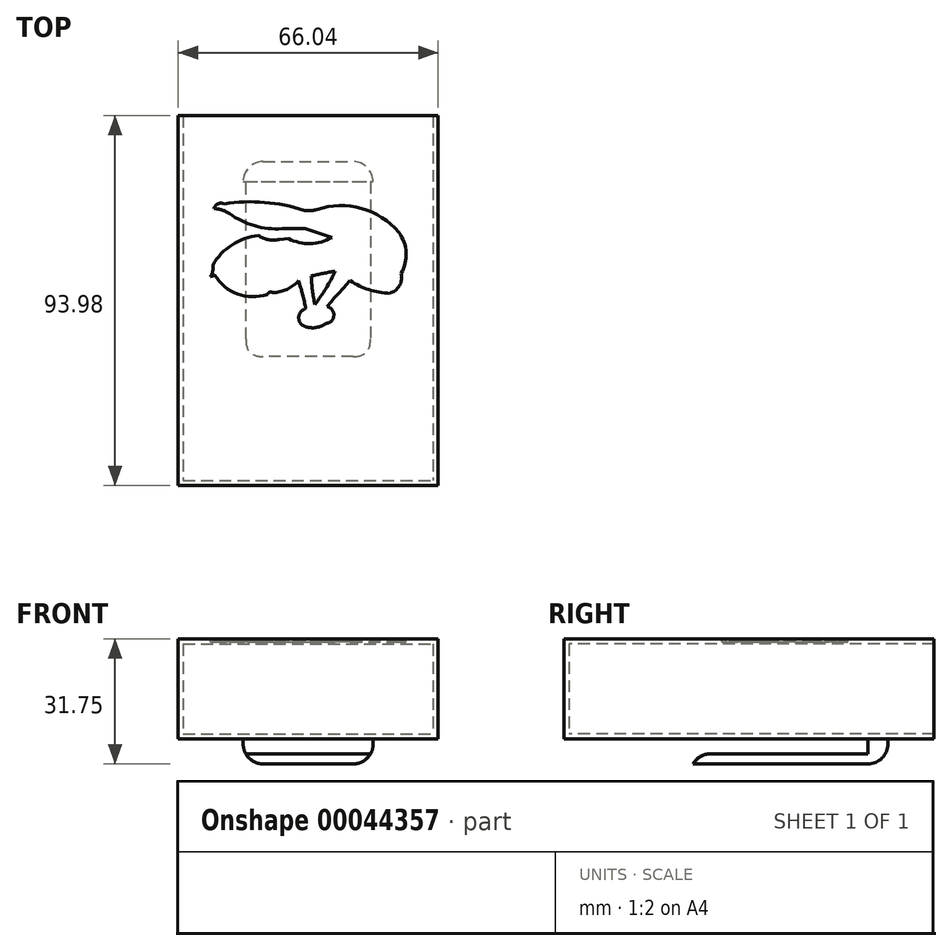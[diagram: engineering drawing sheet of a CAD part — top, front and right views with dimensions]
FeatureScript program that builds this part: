
annotation { "Feature Type Name" : "Feature", "Feature Type Description" : "" }
export const myFeature = defineFeature(function(context is Context, id is Id, definition is map)
    precondition{}
    {
        {
            var Q0;
            Q0=qCreatedBy(makeId("Top.planeOp"),FACE);
            var sketch = newSketch(context, id + "F0", { "sketchPlane" : qUnion([Q0])});
            skPoint(sketch, "E0", {"position": v(0, 0) * mm});
            skPoint(sketch, "E1", {"position": v(66.04, 0) * mm});
            skPoint(sketch, "E2", {"position": v(0, 93.98) * mm});
            skLineSegment(sketch, "E3.bottom", {"start": v(0, 93.98) * mm, "end": v(66.04, 93.98) * mm});
            skLineSegment(sketch, "E3.top", {"start": v(0, 0) * mm, "end": v(66.04, 0) * mm});
            skLineSegment(sketch, "E3.left", {"start": v(0, 93.98) * mm, "end": v(0, 0) * mm});
            skLineSegment(sketch, "E3.right", {"start": v(66.04, 93.98) * mm, "end": v(66.04, 0) * mm});
            skSolve(sketch);
        }
        {
            var Q0;
            Q0 = qSketchRegion(id + "F0", true);
            extrude(context, id + "F1", {"entities" : qUnion([Q0]), "depth" : 25.4 * mm});
        }
        {
            var Q0;
            Q0=makeQuery(id+"F1.opExtrude","SWEPT_FACE",FACE,{"disambiguationData":[OSD([sQuery(id+"F0.wireOp",EDGE,"E3.bottom")])]});
            shell(context, id + "F2", {"entities" : qUnion([Q0]), "thickness" : 1.27 * mm});
        }
        {
            var Q0;
            Q0=makeQuery(id+"F1.opExtrude","CAP_FACE",FACE,{"disambiguationData":[OSD([sQuery(id+"F0.wireOp",EDGE,"E3.bottom"),sQuery(id+"F0.wireOp",EDGE,"E3.top"),sQuery(id+"F0.wireOp",EDGE,"E3.left"),sQuery(id+"F0.wireOp",EDGE,"E3.right")])],"isStart":false});
            var sketch = newSketch(context, id + "F3", { "sketchPlane" : qUnion([Q0])});
            skPoint(sketch, "E4", {"position": v(39.02, 63.04) * mm});
            skPoint(sketch, "E5", {"position": v(25.75, 62.49) * mm});
            skPoint(sketch, "E6", {"position": v(20.37, 63.5) * mm});
            skPoint(sketch, "E7", {"position": v(28.02, 62.72) * mm});
            skPoint(sketch, "E8", {"position": v(32.23, 65.22) * mm});
            skPoint(sketch, "E9", {"position": v(13.03, 69.12) * mm});
            skPoint(sketch, "E10", {"position": v(9.05, 70.37) * mm});
            skPoint(sketch, "E11", {"position": v(11.62, 71.54) * mm});
            skPoint(sketch, "E12", {"position": v(32.08, 69.9) * mm});
            skPoint(sketch, "E13", {"position": v(56.04, 64.28) * mm});
            skPoint(sketch, "E14", {"position": v(56.66, 53.9) * mm});
            skPoint(sketch, "E15", {"position": v(53.7, 48.83) * mm});
            skPoint(sketch, "E16", {"position": v(43.7, 52.03) * mm});
            skPoint(sketch, "E17", {"position": v(39.88, 54.45) * mm});
            skPoint(sketch, "E18", {"position": v(33.8, 53.2) * mm});
            skPoint(sketch, "E19", {"position": v(34.73, 45.94) * mm});
            skPoint(sketch, "E20", {"position": v(37.85, 45.47) * mm});
            skPoint(sketch, "E21", {"position": v(37.54, 41.18) * mm});
            skPoint(sketch, "E22", {"position": v(32.39, 44.93) * mm});
            skPoint(sketch, "E23", {"position": v(32.39, 40.32) * mm});
            skPoint(sketch, "E24", {"position": v(30.6, 52.03) * mm});
            skPoint(sketch, "E25", {"position": v(24.04, 48.98) * mm});
            skPoint(sketch, "E26", {"position": v(22.65, 48.57) * mm});
            skPoint(sketch, "E27", {"position": v(9.3, 53.49) * mm});
            skPoint(sketch, "E28", {"position": v(8.22, 53.14) * mm});
            skPoint(sketch, "E29", {"position": v(8.81, 55.98) * mm});
            skArc(sketch, "E30", {"start": v(53.7, 48.83) * mm, "mid": v(56.22, 50.76) * mm, "end": v(56.66, 53.9) * mm});
            skArc(sketch, "E31", {"start": v(43.7, 52.03) * mm, "mid": v(48.48, 49.74) * mm, "end": v(53.7, 48.83) * mm});
            skArc(sketch, "E32", {"start": v(56.66, 53.9) * mm, "mid": v(57.9, 59.19) * mm, "end": v(56.04, 64.28) * mm});
            skPoint(sketch, "E33", {"position": v(35.23, 70.11) * mm});
            skArc(sketch, "E34", {"start": v(56.04, 64.28) * mm, "mid": v(46.53, 70.38) * mm, "end": v(35.23, 70.11) * mm});
            skArc(sketch, "E35", {"start": v(32.08, 69.9) * mm, "mid": v(33.67, 69.82) * mm, "end": v(35.23, 70.11) * mm});
            skArc(sketch, "E36", {"start": v(32.08, 69.9) * mm, "mid": v(21.95, 71.94) * mm, "end": v(11.62, 71.54) * mm});
            skArc(sketch, "E37", {"start": v(11.62, 71.54) * mm, "mid": v(10.07, 71.55) * mm, "end": v(9.05, 70.37) * mm});
            skArc(sketch, "E38", {"start": v(13.03, 69.12) * mm, "mid": v(11.11, 69.98) * mm, "end": v(9.05, 70.37) * mm});
            skArc(sketch, "E39", {"start": v(13.03, 69.12) * mm, "mid": v(19.35, 65.98) * mm, "end": v(26.37, 65.22) * mm});
            skLineSegment(sketch, "E40", {"start": v(26.37, 65.22) * mm, "end": v(32.23, 65.22) * mm});
            skLineSegment(sketch, "E41", {"start": v(32.23, 65.22) * mm, "end": v(39.02, 63.04) * mm});
            skArc(sketch, "E42", {"start": v(28.02, 62.72) * mm, "mid": v(33.56, 61.46) * mm, "end": v(39.02, 63.04) * mm});
            skArc(sketch, "E43", {"start": v(20.37, 63.5) * mm, "mid": v(22.96, 62.45) * mm, "end": v(25.75, 62.49) * mm});
            skLineSegment(sketch, "E44", {"start": v(25.75, 62.49) * mm, "end": v(28.02, 62.72) * mm});
            skArc(sketch, "E45", {"start": v(20.37, 63.5) * mm, "mid": v(13.68, 61.14) * mm, "end": v(8.81, 55.98) * mm});
            skArc(sketch, "E46", {"start": v(8.22, 53.14) * mm, "mid": v(8.76, 54.5) * mm, "end": v(8.81, 55.98) * mm});
            skArc(sketch, "E47", {"start": v(8.22, 53.14) * mm, "mid": v(8.78, 53.24) * mm, "end": v(9.3, 53.49) * mm});
            skArc(sketch, "E48", {"start": v(9.3, 53.49) * mm, "mid": v(15.1, 48.66) * mm, "end": v(22.65, 48.57) * mm});
            skArc(sketch, "E49", {"start": v(24.04, 48.98) * mm, "mid": v(23.25, 49.1) * mm, "end": v(22.65, 48.57) * mm});
            skArc(sketch, "E50", {"start": v(24.04, 48.98) * mm, "mid": v(27.63, 49.83) * mm, "end": v(30.6, 52.03) * mm});
            skArc(sketch, "E51", {"start": v(32.39, 44.93) * mm, "mid": v(30.61, 42.62) * mm, "end": v(32.39, 40.32) * mm});
            skArc(sketch, "E52", {"start": v(37.54, 41.18) * mm, "mid": v(39.54, 43.2) * mm, "end": v(37.85, 45.47) * mm});
            skArc(sketch, "E53", {"start": v(32.39, 40.32) * mm, "mid": v(35.07, 40.13) * mm, "end": v(37.54, 41.18) * mm});
            skArc(sketch, "E54", {"start": v(34.73, 45.94) * mm, "mid": v(37.54, 50.05) * mm, "end": v(39.88, 54.45) * mm});
            skArc(sketch, "E55", {"start": v(33.8, 53.2) * mm, "mid": v(34.12, 49.55) * mm, "end": v(34.73, 45.94) * mm});
            skArc(sketch, "E56", {"start": v(39.88, 54.45) * mm, "mid": v(36.83, 53.88) * mm, "end": v(33.8, 53.2) * mm});
            skArc(sketch, "E57", {"start": v(32.39, 44.93) * mm, "mid": v(31.63, 48.51) * mm, "end": v(30.6, 52.03) * mm});
            skArc(sketch, "E58", {"start": v(43.7, 52.03) * mm, "mid": v(40.73, 48.8) * mm, "end": v(37.85, 45.47) * mm});
            skSolve(sketch);
        }
        {
            var Q0;
            Q0 = qSketchRegion(id + "F3", true);
            extrude(context, id + "F4", {"entities" : qUnion([Q0]), "operationType" : NewBodyOperationType.REMOVE, "oppositeDirection" : true, "depth" : 0.76 * mm});
        }
        {
            var Q0;
            Q0=makeQuery(id+"F1.opExtrude","CAP_FACE",FACE,{"disambiguationData":[OSD([sQuery(id+"F0.wireOp",EDGE,"E3.bottom"),sQuery(id+"F0.wireOp",EDGE,"E3.top"),sQuery(id+"F0.wireOp",EDGE,"E3.left"),sQuery(id+"F0.wireOp",EDGE,"E3.right")])],"isStart":true});
            var sketch = newSketch(context, id + "F5", { "sketchPlane" : qUnion([Q0])});
            skPoint(sketch, "E59", {"position": v(33.02, -82.28) * mm});
            skPoint(sketch, "E59.positionSnap0", {"position": v(33.02, -93.98) * mm});
            skLineSegment(sketch, "E60", {"start": v(33.02, -93.98) * mm, "end": v(0, -93.98) * mm});
            skLineSegment(sketch, "E61", {"start": v(0, -93.98) * mm, "end": v(66.04, -93.98) * mm});
            skLineSegment(sketch, "E62", {"start": v(66.04, -93.98) * mm, "end": v(33.02, -93.98) * mm});
            skPoint(sketch, "E63", {"position": v(49.53, -93.98) * mm});
            skPoint(sketch, "E64", {"position": v(16.51, -82.28) * mm});
            skPoint(sketch, "E64.positionSnap0", {"position": v(16.51, -93.98) * mm});
            skPoint(sketch, "E65", {"position": v(49.53, -82.28) * mm});
            skPoint(sketch, "E66", {"position": v(49.53, -77.2) * mm});
            skLineSegment(sketch, "E67.bottom", {"start": v(16.51, -82.28) * mm, "end": v(49.53, -82.28) * mm});
            skLineSegment(sketch, "E67.top", {"start": v(16.51, -77.2) * mm, "end": v(49.53, -77.2) * mm});
            skLineSegment(sketch, "E67.left", {"start": v(16.51, -82.28) * mm, "end": v(16.51, -77.2) * mm});
            skLineSegment(sketch, "E67.right", {"start": v(49.53, -82.28) * mm, "end": v(49.53, -77.2) * mm});
            skSolve(sketch);
        }
        {
            var Q0;
            Q0 = qSketchRegion(id + "F5", true);
            extrude(context, id + "F6", {"entities" : qUnion([Q0]), "operationType" : NewBodyOperationType.ADD, "depth" : 3.8 * mm});
        }
        {
            var Q0;
            Q0=makeQuery(id+"F6.opExtrude","CAP_FACE",FACE,{"disambiguationData":[OSD([sQuery(id+"F5.wireOp",EDGE,"E67.bottom"),sQuery(id+"F5.wireOp",EDGE,"E67.top"),sQuery(id+"F5.wireOp",EDGE,"E67.left"),sQuery(id+"F5.wireOp",EDGE,"E67.right")])],"isStart":false});
            var sketch = newSketch(context, id + "F7", { "sketchPlane" : qUnion([Q0])});
            skPoint(sketch, "E68", {"position": v(49.53, -32.75) * mm});
            skLineSegment(sketch, "E69.bottom", {"start": v(49.53, -32.75) * mm, "end": v(16.51, -32.75) * mm});
            skLineSegment(sketch, "E69.top", {"start": v(49.53, -82.28) * mm, "end": v(16.51, -82.28) * mm});
            skLineSegment(sketch, "E69.left", {"start": v(49.53, -32.75) * mm, "end": v(49.53, -82.28) * mm});
            skLineSegment(sketch, "E69.right", {"start": v(16.51, -32.75) * mm, "end": v(16.51, -82.28) * mm});
            skSolve(sketch);
        }
        {
            var Q0;
            Q0 = qSketchRegion(id + "F7", true);
            extrude(context, id + "F8", {"entities" : qUnion([Q0]), "operationType" : NewBodyOperationType.ADD, "depth" : 2.54 * mm});
        }
        {
            var Q0;
            Q0=makeQuery(id+"F8.opExtrude","CAP_EDGE",EDGE,{"disambiguationData":[OSD([sQuery(id+"F7.wireOp",EDGE,"E69.bottom")])],"isStart":true});
            var Q1;
            Q1=makeQuery(id+"F6.opExtrude","CAP_EDGE",EDGE,{"disambiguationData":[OSD([sQuery(id+"F5.wireOp",EDGE,"E67.top")])],"isStart":false});
            fillet(context, id + "F9", {"entities" : qUnion([Q0, Q1]), "radius" : 5.08 * mm, "tangentPropagation" : true, "allowEdgeOverflow" : false});
        }
        {
            var Q0;
            Q0=makeQuery(id+"F8.boolean.opBoolean","MERGE",EDGE,{"derivedFrom":[makeQuery(id+"F6.opExtrude","SWEPT_EDGE",EDGE,{"disambiguationData":[OSD([sQuery(id+"F5.wireOp",EDGE,"E67.bottom"),sQuery(id+"F5.wireOp",EDGE,"E67.right")])]}),makeQuery(id+"F8.opExtrude","SWEPT_EDGE",EDGE,{"disambiguationData":[OSD([sQuery(id+"F7.wireOp",EDGE,"E69.top"),sQuery(id+"F7.wireOp",EDGE,"E69.left")])]})]});
            var Q1;
            Q1=makeQuery(id+"F8.opExtrude","CAP_EDGE",EDGE,{"disambiguationData":[OSD([sQuery(id+"F7.wireOp",EDGE,"E69.top")])],"isStart":false});
            var Q2;
            Q2=makeQuery(id+"F8.opExtrude","CAP_EDGE",EDGE,{"disambiguationData":[OSD([sQuery(id+"F7.wireOp",EDGE,"E69.left")])],"isStart":false});
            var Q3;
            Q3=makeQuery(id+"F8.opExtrude","CAP_EDGE",EDGE,{"disambiguationData":[OSD([sQuery(id+"F7.wireOp",EDGE,"E69.right")])],"isStart":false});
            var Q4;
            Q4=makeQuery(id+"F8.boolean.opBoolean","MERGE",EDGE,{"derivedFrom":[makeQuery(id+"F6.opExtrude","SWEPT_EDGE",EDGE,{"disambiguationData":[OSD([sQuery(id+"F5.wireOp",EDGE,"E67.bottom"),sQuery(id+"F5.wireOp",EDGE,"E67.left")])]}),makeQuery(id+"F8.opExtrude","SWEPT_EDGE",EDGE,{"disambiguationData":[OSD([sQuery(id+"F7.wireOp",EDGE,"E69.top"),sQuery(id+"F7.wireOp",EDGE,"E69.right")])]})]});
            fillet(context, id + "F10", {"entities" : qUnion([Q0, Q1, Q2, Q3, Q4]), "radius" : 5.08 * mm, "tangentPropagation" : true, "allowEdgeOverflow" : false});
        }
    });
